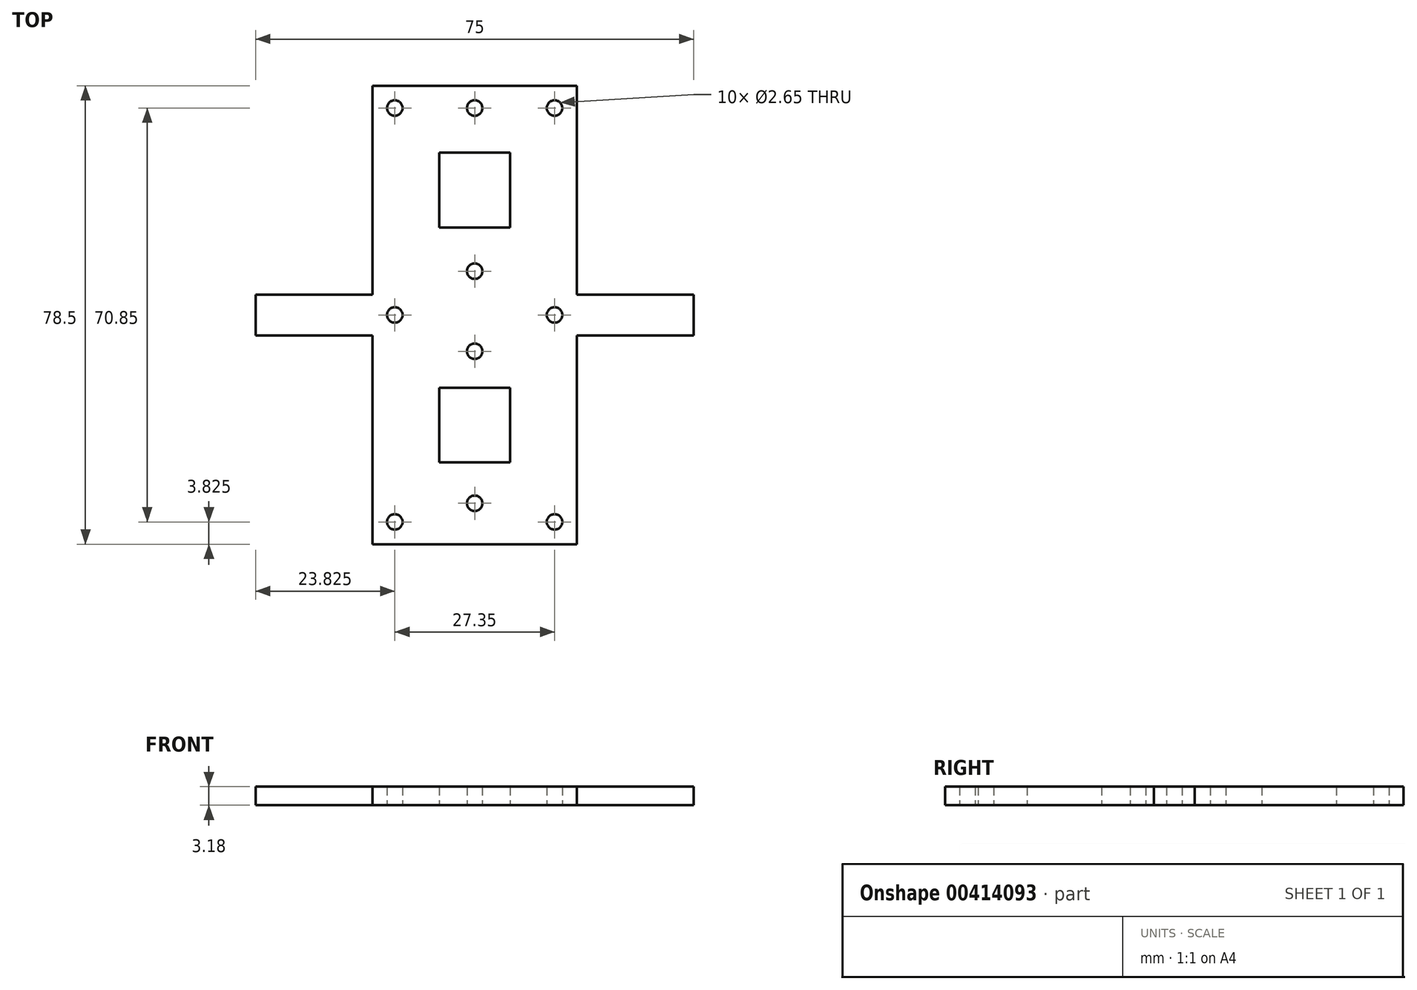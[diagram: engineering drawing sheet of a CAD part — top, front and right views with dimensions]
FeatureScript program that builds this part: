
annotation { "Feature Type Name" : "Feature", "Feature Type Description" : "" }
export const myFeature = defineFeature(function(context is Context, id is Id, definition is map)
    precondition{}
    {
        {
            var Q0;
            Q0=qCreatedBy(makeId("Top.planeOp"),FACE);
            var sketch = newSketch(context, id + "F0", { "sketchPlane" : qUnion([Q0])});
            skLineSegment(sketch, "E0.bottom", {"start": v(0, 0) * mm, "end": v(44.5, 0) * mm});
            skLineSegment(sketch, "E0.top", {"start": v(0, 78.5) * mm, "end": v(44.5, 78.5) * mm});
            skLineSegment(sketch, "E0.left", {"start": v(0, 0) * mm, "end": v(0, 35.75) * mm});
            skLineSegment(sketch, "E0.right", {"start": v(44.5, 0) * mm, "end": v(44.5, 35.75) * mm});
            skLineSegment(sketch, "E1.top", {"start": v(-20, 35.75) * mm, "end": v(0, 35.75) * mm});
            skLineSegment(sketch, "E1.left", {"start": v(-20, 39.25) * mm, "end": v(-20, 35.75) * mm});
            skLineSegment(sketch, "E2.top", {"start": v(-20, 42.75) * mm, "end": v(0, 42.75) * mm});
            skLineSegment(sketch, "E2.left", {"start": v(-20, 39.25) * mm, "end": v(-20, 42.75) * mm});
            skLineSegment(sketch, "E3.top", {"start": v(64.5, 42.75) * mm, "end": v(44.5, 42.75) * mm});
            skLineSegment(sketch, "E3.left", {"start": v(64.5, 39.25) * mm, "end": v(64.5, 42.75) * mm});
            skLineSegment(sketch, "E4.top", {"start": v(64.5, 35.75) * mm, "end": v(44.5, 35.75) * mm});
            skLineSegment(sketch, "E4.left", {"start": v(64.5, 39.25) * mm, "end": v(64.5, 35.75) * mm});
            skLineSegment(sketch, "E5.trimOffspring", {"start": v(0, 42.75) * mm, "end": v(0, 78.5) * mm});
            skPoint(sketch, "E6.orphan", {"position": v(0, 39.25) * mm});
            skLineSegment(sketch, "E7.trimOffspring", {"start": v(44.5, 42.75) * mm, "end": v(44.5, 78.5) * mm});
            skPoint(sketch, "E8.start.orphan", {"position": v(44.5, 39.25) * mm});
            skLineSegment(sketch, "E9.bottom", {"start": v(11.12, 69.56) * mm, "end": v(33.37, 69.56) * mm});
            skLineSegment(sketch, "E9.top", {"start": v(11.12, 51.69) * mm, "end": v(33.37, 51.69) * mm});
            skLineSegment(sketch, "E9.left", {"start": v(11.12, 69.56) * mm, "end": v(11.12, 51.69) * mm});
            skLineSegment(sketch, "E9.right", {"start": v(33.37, 69.56) * mm, "end": v(33.37, 51.69) * mm});
            skLineSegment(sketch, "E10.bottom", {"start": v(11.13, 26.81) * mm, "end": v(33.38, 26.81) * mm});
            skLineSegment(sketch, "E10.top", {"start": v(11.13, 8.94) * mm, "end": v(33.38, 8.94) * mm});
            skLineSegment(sketch, "E10.left", {"start": v(11.13, 26.81) * mm, "end": v(11.13, 8.94) * mm});
            skLineSegment(sketch, "E10.right", {"start": v(33.38, 26.81) * mm, "end": v(33.38, 8.94) * mm});
            skPoint(sketch, "E11.orphan", {"position": v(22.25, 17.88) * mm});
            skPoint(sketch, "E12.start.orphan", {"position": v(22.25, 60.62) * mm});
            skSolve(sketch);
        }
        {
            var Q0;
            Q0=makeQuery(id+"F0.imprint","IMPRINT",FACE,{"disambiguationData":[TD([[makeQuery(id+"F0.imprint","IMPRINT",EDGE,{"derivedFrom":sQuery(id+"F0.wireOp",EDGE,"E0.bottom")}),1.0]])]});
            extrude(context, id + "F1", {"entities" : qUnion([Q0]), "depth" : 3.17 * mm});
        }
        {
            var Q0;
            Q0=makeQuery(id+"F1.opExtrude","SWEPT_FACE",FACE,{"disambiguationData":[OSD([sQuery(id+"F0.wireOp",EDGE,"E9.bottom")])]});
            extrude(context, id + "F2", {"entities" : qUnion([Q0]), "operationType" : NewBodyOperationType.ADD, "depth" : 5.08 * mm});
        }
        {
            var Q0;
            Q0=makeQuery(id+"F1.opExtrude","SWEPT_FACE",FACE,{"disambiguationData":[OSD([sQuery(id+"F0.wireOp",EDGE,"E9.top")])]});
            var Q1;
            Q1=makeQuery(id+"F1.opExtrude","SWEPT_FACE",FACE,{"disambiguationData":[OSD([sQuery(id+"F0.wireOp",EDGE,"E10.bottom")])]});
            extrude(context, id + "F3", {"entities" : qUnion([Q0, Q1]), "operationType" : NewBodyOperationType.ADD, "depth" : 2.54 * mm});
        }
        {
            var Q0;
            Q0=makeQuery(id+"F1.opExtrude","SWEPT_FACE",FACE,{"disambiguationData":[OSD([sQuery(id+"F0.wireOp",EDGE,"E10.top")])]});
            extrude(context, id + "F4", {"entities" : qUnion([Q0]), "operationType" : NewBodyOperationType.ADD, "depth" : 5.08 * mm});
        }
        {
            var Q0;
            Q0=makeQuery(id+"F1.opExtrude","SWEPT_FACE",FACE,{"disambiguationData":[OSD([sQuery(id+"F0.wireOp",EDGE,"E9.right")])]});
            var Q1;
            Q1=makeQuery(id+"F1.opExtrude","SWEPT_FACE",FACE,{"disambiguationData":[OSD([sQuery(id+"F0.wireOp",EDGE,"E10.right")])]});
            extrude(context, id + "F5", {"entities" : qUnion([Q0, Q1]), "operationType" : NewBodyOperationType.ADD, "depth" : 5.08 * mm});
        }
        {
            var Q0;
            Q0=makeQuery(id+"F1.opExtrude","SWEPT_FACE",FACE,{"disambiguationData":[OSD([sQuery(id+"F0.wireOp",EDGE,"E9.left")])]});
            var Q1;
            Q1=makeQuery(id+"F1.opExtrude","SWEPT_FACE",FACE,{"disambiguationData":[OSD([sQuery(id+"F0.wireOp",EDGE,"E10.left")])]});
            extrude(context, id + "F6", {"entities" : qUnion([Q0, Q1]), "operationType" : NewBodyOperationType.ADD, "depth" : 5.08 * mm});
        }
        {
            var Q0;
            Q0=makeQuery(id+"F1.opExtrude","SWEPT_FACE",FACE,{"disambiguationData":[OSD([sQuery(id+"F0.wireOp",EDGE,"E7.trimOffspring")])]});
            var Q1;
            Q1=makeQuery(id+"F1.opExtrude","SWEPT_FACE",FACE,{"disambiguationData":[OSD([sQuery(id+"F0.wireOp",EDGE,"E0.right")])]});
            extrude(context, id + "F7", {"entities" : qUnion([Q0, Q1]), "operationType" : NewBodyOperationType.REMOVE, "oppositeDirection" : true, "depth" : 4.75 * mm});
        }
        {
            var Q0;
            Q0=makeQuery(id+"F1.opExtrude","SWEPT_FACE",FACE,{"disambiguationData":[OSD([sQuery(id+"F0.wireOp",EDGE,"E5.trimOffspring")])]});
            var Q1;
            Q1=makeQuery(id+"F1.opExtrude","SWEPT_FACE",FACE,{"disambiguationData":[OSD([sQuery(id+"F0.wireOp",EDGE,"E0.left")])]});
            extrude(context, id + "F8", {"entities" : qUnion([Q0, Q1]), "operationType" : NewBodyOperationType.REMOVE, "oppositeDirection" : true, "depth" : 4.75 * mm});
        }
        {
            var Q0;
            Q0=makeQuery(id+"F1.opExtrude","SWEPT_FACE",FACE,{"disambiguationData":[OSD([sQuery(id+"F0.wireOp",EDGE,"E1.left"),sQuery(id+"F0.wireOp",EDGE,"E2.left")])]});
            extrude(context, id + "F9", {"entities" : qUnion([Q0]), "operationType" : NewBodyOperationType.REMOVE, "oppositeDirection" : true, "depth" : 2 * 2.37 * mm});
        }
        {
            var Q0;
            Q0=makeQuery(id+"F1.opExtrude","SWEPT_FACE",FACE,{"disambiguationData":[OSD([sQuery(id+"F0.wireOp",EDGE,"E3.left"),sQuery(id+"F0.wireOp",EDGE,"E4.left")])]});
            extrude(context, id + "F10", {"entities" : qUnion([Q0]), "operationType" : NewBodyOperationType.REMOVE, "oppositeDirection" : true, "depth" : 2 * 2.37 * mm});
        }
        {
            var Q0;
            Q0=makeQuery(id+"F2.opExtrude","CAP_FACE",FACE,{"disambiguationData":[OSD([sQuery(id+"F0.wireOp",EDGE,"E9.bottom")])],"isStart":false});
            extrude(context, id + "F11", {"entities" : qUnion([Q0]), "operationType" : NewBodyOperationType.REMOVE, "oppositeDirection" : true, "depth" : 2.54 * mm});
        }
        {
            var Q0;
            {var subQ0=sQuery(id+"F0.wireOp",EDGE,"E10.left");var subQ1=sQuery(id+"F0.wireOp",EDGE,"E9.left");var subQ2=sQuery(id+"F0.wireOp",EDGE,"E10.right");var subQ3=sQuery(id+"F0.wireOp",EDGE,"E9.right");var subQ4=sQuery(id+"F0.wireOp",EDGE,"E10.top");var subQ5=sQuery(id+"F0.wireOp",EDGE,"E9.top");var subQ6=sQuery(id+"F0.wireOp",EDGE,"E9.bottom");Q0=makeQuery(id+"F6.boolean.opBoolean","MERGE",FACE,{"derivedFrom":[makeQuery(id+"F5.boolean.opBoolean","MERGE",FACE,{"derivedFrom":[makeQuery(id+"F4.boolean.opBoolean","MERGE",FACE,{"derivedFrom":[makeQuery(id+"F3.boolean.opBoolean","MERGE",FACE,{"derivedFrom":[makeQuery(id+"F2.boolean.opBoolean","MERGE",FACE,{"derivedFrom":[makeQuery(id+"F1.opExtrude","CAP_FACE",FACE,{"disambiguationData":[OSD([sQuery(id+"F0.wireOp",EDGE,"E0.bottom"),sQuery(id+"F0.wireOp",EDGE,"E0.top"),sQuery(id+"F0.wireOp",EDGE,"E0.left"),sQuery(id+"F0.wireOp",EDGE,"E0.right"),sQuery(id+"F0.wireOp",EDGE,"E1.top"),sQuery(id+"F0.wireOp",EDGE,"E1.left"),sQuery(id+"F0.wireOp",EDGE,"E2.top"),sQuery(id+"F0.wireOp",EDGE,"E2.left"),sQuery(id+"F0.wireOp",EDGE,"E3.top"),sQuery(id+"F0.wireOp",EDGE,"E3.left"),sQuery(id+"F0.wireOp",EDGE,"E4.top"),sQuery(id+"F0.wireOp",EDGE,"E4.left"),sQuery(id+"F0.wireOp",EDGE,"E5.trimOffspring"),sQuery(id+"F0.wireOp",EDGE,"E7.trimOffspring"),subQ6,subQ5,subQ1,subQ3,sQuery(id+"F0.wireOp",EDGE,"E10.bottom"),subQ4,subQ0,subQ2])],"isStart":true}),makeQuery(id+"F2.opExtrude","SWEPT_FACE",FACE,{"disambiguationData":[OSD([subQ6]),TDD([makeQuery(id+"F1.opExtrude","CAP_EDGE",EDGE,{"disambiguationData":[OSD([subQ6])],"isStart":true})])]})]}),makeQuery(id+"F3.opExtrude","SWEPT_FACE",FACE,{"disambiguationData":[OSD([subQ5]),TDD([makeQuery(id+"F1.opExtrude","CAP_EDGE",EDGE,{"disambiguationData":[OSD([subQ5])],"isStart":true})])]})]}),makeQuery(id+"F4.opExtrude","SWEPT_FACE",FACE,{"disambiguationData":[OSD([subQ4]),TDD([makeQuery(id+"F1.opExtrude","CAP_EDGE",EDGE,{"disambiguationData":[OSD([subQ4])],"isStart":true})])]})]}),makeQuery(id+"F5.opExtrude","SWEPT_FACE",FACE,{"disambiguationData":[OSD([subQ3]),TDD([makeQuery(id+"F1.opExtrude","CAP_EDGE",EDGE,{"disambiguationData":[OSD([subQ3])],"isStart":true})])]}),makeQuery(id+"F5.opExtrude","SWEPT_FACE",FACE,{"disambiguationData":[OSD([subQ2]),TDD([makeQuery(id+"F1.opExtrude","CAP_EDGE",EDGE,{"disambiguationData":[OSD([subQ2])],"isStart":true})])]})]}),makeQuery(id+"F6.opExtrude","SWEPT_FACE",FACE,{"disambiguationData":[OSD([subQ1]),TDD([makeQuery(id+"F1.opExtrude","CAP_EDGE",EDGE,{"disambiguationData":[OSD([subQ1])],"isStart":true})])]}),makeQuery(id+"F6.opExtrude","SWEPT_FACE",FACE,{"disambiguationData":[OSD([subQ0]),TDD([makeQuery(id+"F1.opExtrude","CAP_EDGE",EDGE,{"disambiguationData":[OSD([subQ0])],"isStart":true})])]})]});}
            var sketch = newSketch(context, id + "F12", { "sketchPlane" : qUnion([Q0])});
            skLineSegment(sketch, "E13.bottom", {"start": v(39.75, -78.5) * mm, "end": v(37.25, -78.5) * mm});
            skLineSegment(sketch, "E13.left", {"start": v(39.75, -78.5) * mm, "end": v(39.75, -76) * mm});
            skLineSegment(sketch, "E14.bottom", {"start": v(4.75, 0) * mm, "end": v(7.25, 0) * mm});
            skLineSegment(sketch, "E14.left", {"start": v(4.75, 0) * mm, "end": v(4.75, -2.5) * mm});
            skCircle(sketch, "E15", {"center": v(35.93, -74.67) * mm, "radius": 1.33 * mm});
            skCircle(sketch, "E16", {"center": v(8.57, -74.67) * mm, "radius": 1.33 * mm});
            skCircle(sketch, "E17", {"center": v(8.57, -3.83) * mm, "radius": 1.32 * mm});
            skCircle(sketch, "E18", {"center": v(35.93, -3.83) * mm, "radius": 1.32 * mm});
            skCircle(sketch, "E19", {"center": v(35.93, -39.25) * mm, "radius": 1.33 * mm});
            skCircle(sketch, "E20", {"center": v(8.57, -39.25) * mm, "radius": 1.32 * mm});
            skPoint(sketch, "E21.orphan", {"position": v(-15.25, -39.25) * mm});
            skPoint(sketch, "E22.right.start.orphan", {"position": v(9.9, -39.25) * mm});
            skPoint(sketch, "E23.orphan", {"position": v(7.25, -39.25) * mm});
            skPoint(sketch, "E24.top.end.orphan", {"position": v(9.9, -5.15) * mm});
            skPoint(sketch, "E25.orphan", {"position": v(7.25, -2.5) * mm});
            skPoint(sketch, "E26.top.start.orphan", {"position": v(37.25, -2.5) * mm});
            skPoint(sketch, "E27.orphan", {"position": v(34.6, -5.15) * mm});
            skPoint(sketch, "E28.orphan", {"position": v(59.75, -39.25) * mm});
            skPoint(sketch, "E29.orphan", {"position": v(7.25, -76) * mm});
            skPoint(sketch, "E30.orphan", {"position": v(37.25, -39.25) * mm});
            skPoint(sketch, "E22.left.end.orphan", {"position": v(34.6, -39.25) * mm});
            skPoint(sketch, "E31.orphan", {"position": v(34.6, -73.35) * mm});
            skPoint(sketch, "E32.orphan", {"position": v(37.25, -76) * mm});
            skPoint(sketch, "E33.start.orphan", {"position": v(9.9, -73.35) * mm});
            skLineSegment(sketch, "E34", {"start": v(8.57, -39.25) * mm, "end": v(9.9, -39.25) * mm});
            skLineSegment(sketch, "E35", {"start": v(8.57, -74.67) * mm, "end": v(9.9, -74.67) * mm});
            skCircle(sketch, "E36", {"center": v(22.25, -74.67) * mm, "radius": 1.32 * mm});
            skLineSegment(sketch, "E37.trimOffspring", {"start": v(22.25, -74.67) * mm, "end": v(23.57, -74.67) * mm});
            skLineSegment(sketch, "E38.trimOffspring", {"start": v(34.6, -74.67) * mm, "end": v(35.93, -74.67) * mm});
            skLineSegment(sketch, "E39.trimOffspring", {"start": v(34.6, -39.25) * mm, "end": v(35.93, -39.25) * mm});
            skPoint(sketch, "E40.center.orphan", {"position": v(22.25, -39.25) * mm});
            skPoint(sketch, "E41", {"position": v(22.25, -7) * mm});
            skPoint(sketch, "E42", {"position": v(22.25, -33.03) * mm});
            skPoint(sketch, "E43", {"position": v(22.25, -46.74) * mm});
            skCircle(sketch, "E44", {"center": v(22.25, -46.74) * mm, "radius": 1.32 * mm});
            skCircle(sketch, "E45", {"center": v(22.25, -7) * mm, "radius": 1.32 * mm});
            skPoint(sketch, "E46.trimOffspring.end.orphan", {"position": v(22.25, -54.23) * mm});
            skPoint(sketch, "E47.orphan", {"position": v(22.25, -26.81) * mm});
            skPoint(sketch, "E48.orphan", {"position": v(22.25, 0) * mm});
            skPoint(sketch, "E49.orphan", {"position": v(22.25, -14.02) * mm});
            skCircle(sketch, "E50", {"center": v(22.25, -33.03) * mm, "radius": 1.32 * mm});
            skSolve(sketch);
        }
        {
            var Q0;
            Q0=makeQuery(id+"F12.imprint","IMPRINT",FACE,{"disambiguationData":[TD([[makeQuery(id+"F12.imprint","IMPRINT",EDGE,{"derivedFrom":sQuery(id+"F12.wireOp",EDGE,"E15")}),1.0]])]});
            var Q1;
            Q1=makeQuery(id+"F12.imprint","IMPRINT",FACE,{"disambiguationData":[TD([[makeQuery(id+"F12.imprint","IMPRINT",EDGE,{"derivedFrom":sQuery(id+"F12.wireOp",EDGE,"E16")}),1.0]])]});
            var Q2;
            Q2=makeQuery(id+"F12.imprint","IMPRINT",FACE,{"disambiguationData":[TD([[makeQuery(id+"F12.imprint","IMPRINT",EDGE,{"derivedFrom":sQuery(id+"F12.wireOp",EDGE,"E20")}),1.0]])]});
            var Q3;
            Q3=makeQuery(id+"F12.imprint","IMPRINT",FACE,{"disambiguationData":[TD([[makeQuery(id+"F12.imprint","IMPRINT",EDGE,{"derivedFrom":sQuery(id+"F12.wireOp",EDGE,"E19")}),1.0]])]});
            var Q4;
            Q4=makeQuery(id+"F12.imprint","IMPRINT",FACE,{"disambiguationData":[TD([[makeQuery(id+"F12.imprint","IMPRINT",EDGE,{"derivedFrom":sQuery(id+"F12.wireOp",EDGE,"E18")}),1.0]])]});
            var Q5;
            Q5=makeQuery(id+"F12.imprint","IMPRINT",FACE,{"disambiguationData":[TD([[makeQuery(id+"F12.imprint","IMPRINT",EDGE,{"derivedFrom":sQuery(id+"F12.wireOp",EDGE,"E17")}),1.0]])]});
            extrude(context, id + "F13", {"entities" : qUnion([Q0, Q1, Q2, Q3, Q4, Q5]), "operationType" : NewBodyOperationType.REMOVE, "oppositeDirection" : true, "depth" : 25.4 * mm});
        }
        {
            var Q0;
            Q0=makeQuery(id+"F12.imprint","IMPRINT",FACE,{"disambiguationData":[TD([[makeQuery(id+"F12.imprint","IMPRINT",EDGE,{"derivedFrom":sQuery(id+"F12.wireOp",EDGE,"E36")}),1.0]])]});
            var Q1;
            Q1=makeQuery(id+"F12.imprint","IMPRINT",FACE,{"disambiguationData":[TD([[makeQuery(id+"F12.imprint","IMPRINT",EDGE,{"derivedFrom":sQuery(id+"F12.wireOp",EDGE,"E40")}),1.0]])]});
            extrude(context, id + "F14", {"entities" : qUnion([Q0, Q1]), "operationType" : NewBodyOperationType.REMOVE, "oppositeDirection" : true, "depth" : 25.4 * mm});
        }
        {
            var Q0;
            Q0=makeQuery(id+"F12.imprint","IMPRINT",FACE,{"disambiguationData":[TD([[makeQuery(id+"F12.imprint","IMPRINT",EDGE,{"derivedFrom":sQuery(id+"F12.wireOp",EDGE,"E45")}),1.0]])]});
            var Q1;
            Q1=makeQuery(id+"F12.imprint","IMPRINT",FACE,{"disambiguationData":[TD([[makeQuery(id+"F12.imprint","IMPRINT",EDGE,{"derivedFrom":sQuery(id+"F12.wireOp",EDGE,"E44")}),1.0]])]});
            extrude(context, id + "F15", {"entities" : qUnion([Q0, Q1]), "operationType" : NewBodyOperationType.REMOVE, "oppositeDirection" : true, "depth" : 25.4 * mm});
        }
        {
            var Q0;
            Q0=makeQuery(id+"F12.imprint","IMPRINT",FACE,{"disambiguationData":[TD([[makeQuery(id+"F12.imprint","IMPRINT",EDGE,{"derivedFrom":sQuery(id+"F12.wireOp",EDGE,"E50")}),1.0]])]});
            extrude(context, id + "F16", {"entities" : qUnion([Q0]), "operationType" : NewBodyOperationType.REMOVE, "oppositeDirection" : true, "depth" : 25.4 * mm});
        }
    });
